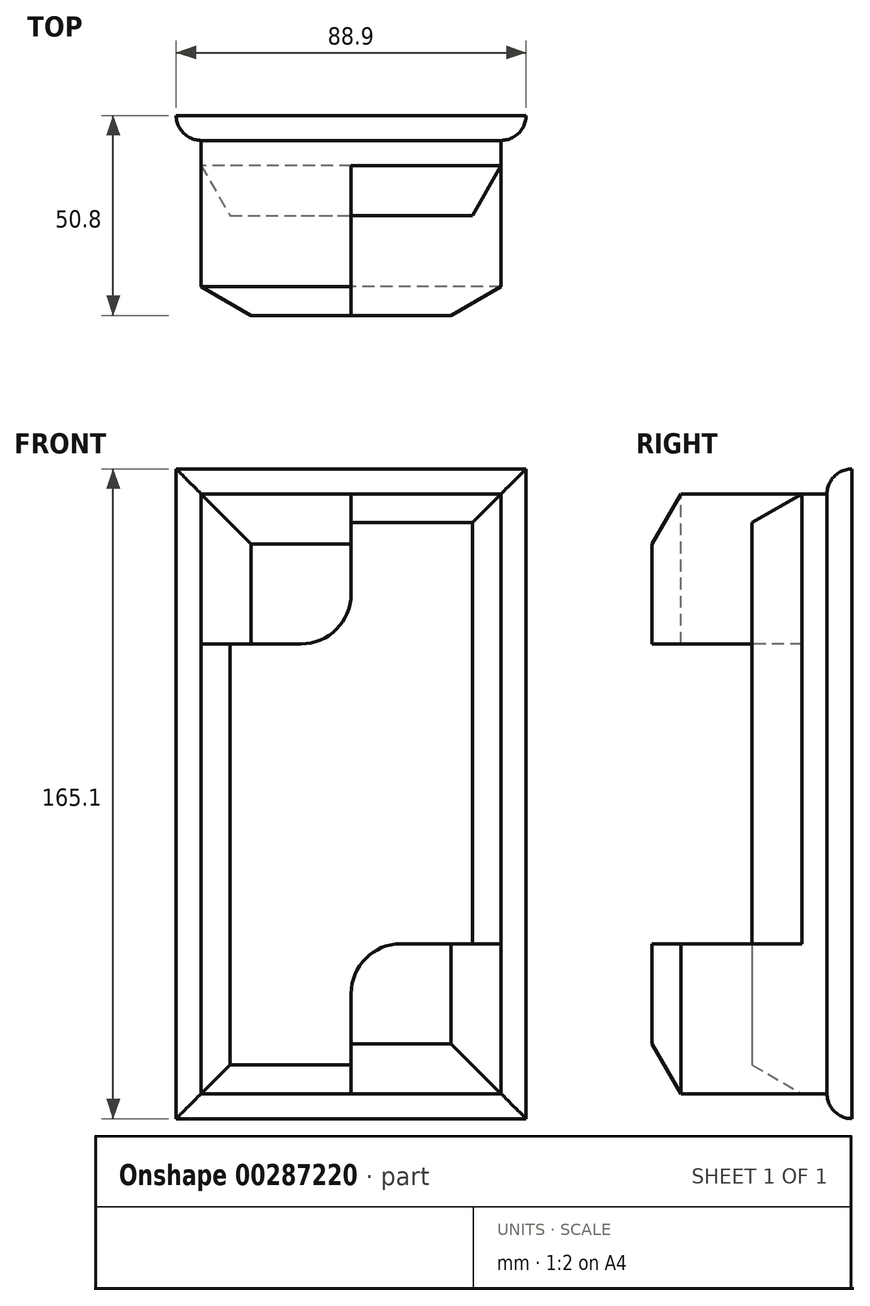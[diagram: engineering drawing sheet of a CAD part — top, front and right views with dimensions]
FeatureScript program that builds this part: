
annotation { "Feature Type Name" : "Feature", "Feature Type Description" : "" }
export const myFeature = defineFeature(function(context is Context, id is Id, definition is map)
    precondition{}
    {
        {
            var Q0;
            Q0=qCreatedBy(makeId("Front.planeOp"),FACE);
            var sketch = newSketch(context, id + "F0", { "sketchPlane" : qUnion([Q0])});
            skLineSegment(sketch, "E0.bottom", {"start": v(-38.1, 76.2) * mm, "end": v(38.1, 76.2) * mm});
            skLineSegment(sketch, "E0.top", {"start": v(-38.1, -76.2) * mm, "end": v(38.1, -76.2) * mm});
            skLineSegment(sketch, "E0.left", {"start": v(-38.1, 76.2) * mm, "end": v(-38.1, -76.2) * mm});
            skLineSegment(sketch, "E0.right", {"start": v(38.1, 76.2) * mm, "end": v(38.1, -76.2) * mm});
            skPoint(sketch, "E0.middle", {"position": v(0, 0) * mm});
            skLineSegment(sketch, "E1.0", {"start": v(-44.45, -82.55) * mm, "end": v(44.45, -82.55) * mm});
            skLineSegment(sketch, "E1.1", {"start": v(-44.45, 82.55) * mm, "end": v(-44.45, -82.55) * mm});
            skLineSegment(sketch, "E1.2", {"start": v(-44.45, 82.55) * mm, "end": v(44.45, 82.55) * mm});
            skLineSegment(sketch, "E1.3", {"start": v(44.45, 82.55) * mm, "end": v(44.45, -82.55) * mm});
            skLineSegment(sketch, "E2", {"start": v(-38.1, 38.1) * mm, "end": v(-12.7, 38.1) * mm});
            skLineSegment(sketch, "E3", {"start": v(0, 50.8) * mm, "end": v(0, 76.2) * mm});
            skLineSegment(sketch, "E4", {"start": v(38.1, -38.1) * mm, "end": v(12.7, -38.1) * mm});
            skLineSegment(sketch, "E5", {"start": v(0, -50.8) * mm, "end": v(0, -76.2) * mm});
            skPoint(sketch, "E6.visualSharp", {"position": v(0, -38.1) * mm});
            skArc(sketch, "E6.filletArc", {"start": v(12.7, -38.1) * mm, "mid": v(3.72, -41.82) * mm, "end": v(0, -50.8) * mm});
            skPoint(sketch, "E7.visualSharp", {"position": v(0, 38.1) * mm});
            skArc(sketch, "E7.filletArc", {"start": v(-12.7, 38.1) * mm, "mid": v(-3.72, 41.82) * mm, "end": v(0, 50.8) * mm});
            skSolve(sketch);
        }
        {
            var Q0;
            Q0 = qSketchRegion(id + "F0", true);
            extrude(context, id + "F1", {"entities" : qUnion([Q0]), "depth" : 6.35 * mm});
        }
        {
            var Q0;
            {var subQ3=sQuery(id+"F0.wireOp",EDGE,"E2");Q0=makeQuery(id+"F0.imprint","IMPRINT",FACE,{"disambiguationData":[TD([[makeQuery(id+"F0.imprint","IMPRINT",EDGE,{"derivedFrom":subQ3}),-1.0]])]});}
            extrude(context, id + "F2", {"entities" : qUnion([Q0]), "operationType" : NewBodyOperationType.ADD, "depth" : 25.4 * mm});
        }
        {
            var Q0;
            {var subQ1=sQuery(id+"F0.wireOp",EDGE,"E2");Q0=makeQuery(id+"F0.imprint","IMPRINT",FACE,{"disambiguationData":[TD([[makeQuery(id+"F0.imprint","IMPRINT",EDGE,{"derivedFrom":subQ1}),1.0]])]});}
            var Q1;
            {var subQ1=sQuery(id+"F0.wireOp",EDGE,"E4");Q1=makeQuery(id+"F0.imprint","IMPRINT",FACE,{"disambiguationData":[TD([[makeQuery(id+"F0.imprint","IMPRINT",EDGE,{"derivedFrom":subQ1}),1.0]])]});}
            extrude(context, id + "F3", {"entities" : qUnion([Q0, Q1]), "operationType" : NewBodyOperationType.ADD, "depth" : 50.8 * mm});
        }
        {
            var Q0;
            Q0=makeQuery(id+"F3.opExtrude","CAP_EDGE",EDGE,{"disambiguationData":[OSD([sQuery(id+"F0.wireOp",EDGE,"E0.left")])],"isStart":false});
            var Q1;
            Q1=makeQuery(id+"F3.opExtrude","CAP_EDGE",EDGE,{"disambiguationData":[OSD([sQuery(id+"F0.wireOp",EDGE,"E0.top")])],"isStart":false});
            var Q2;
            Q2=makeQuery(id+"F3.opExtrude","CAP_EDGE",EDGE,{"disambiguationData":[OSD([sQuery(id+"F0.wireOp",EDGE,"E0.bottom")])],"isStart":false});
            chamfer(context, id + "F4", {"entities" : qUnion([Q0, Q1, Q2]), "chamferType" : ChamferType.OFFSET_ANGLE, "width" : 12.7 * mm, "oppositeDirection" : false, "angle" : 30 * degree, "tangentPropagation" : true});
        }
        {
            var Q0;
            Q0=makeQuery(id+"F1.opExtrude","CAP_EDGE",EDGE,{"disambiguationData":[OSD([sQuery(id+"F0.wireOp",EDGE,"E1.3")])],"isStart":false});
            var Q1;
            Q1=makeQuery(id+"F1.opExtrude","CAP_EDGE",EDGE,{"disambiguationData":[OSD([sQuery(id+"F0.wireOp",EDGE,"E1.2")])],"isStart":false});
            var Q2;
            Q2=makeQuery(id+"F1.opExtrude","CAP_EDGE",EDGE,{"disambiguationData":[OSD([sQuery(id+"F0.wireOp",EDGE,"E1.1")])],"isStart":false});
            var Q3;
            Q3=makeQuery(id+"F1.opExtrude","CAP_EDGE",EDGE,{"disambiguationData":[OSD([sQuery(id+"F0.wireOp",EDGE,"E1.0")])],"isStart":false});
            fillet(context, id + "F5", {"entities" : qUnion([Q0, Q1, Q2, Q3]), "radius" : 6.35 * mm, "tangentPropagation" : true, "allowEdgeOverflow" : false});
        }
        {
            var Q0;
            Q0=makeQuery(id+"F2.opExtrude","CAP_EDGE",EDGE,{"disambiguationData":[OSD([sQuery(id+"F0.wireOp",EDGE,"E0.right")])],"isStart":false});
            var Q1;
            Q1=makeQuery(id+"F2.opExtrude","CAP_EDGE",EDGE,{"disambiguationData":[OSD([sQuery(id+"F0.wireOp",EDGE,"E0.bottom")])],"isStart":false});
            var Q2;
            Q2=makeQuery(id+"F2.opExtrude","CAP_EDGE",EDGE,{"disambiguationData":[OSD([sQuery(id+"F0.wireOp",EDGE,"E0.left")])],"isStart":false});
            var Q3;
            Q3=makeQuery(id+"F2.opExtrude","CAP_EDGE",EDGE,{"disambiguationData":[OSD([sQuery(id+"F0.wireOp",EDGE,"E0.top")])],"isStart":false});
            chamfer(context, id + "F6", {"entities" : qUnion([Q0, Q1, Q2, Q3]), "chamferType" : ChamferType.OFFSET_ANGLE, "width" : 12.7 * mm, "oppositeDirection" : false, "angle" : 30 * degree, "tangentPropagation" : true});
        }
        {
            var Q0;
            Q0=makeQuery(id+"F3.opExtrude","CAP_EDGE",EDGE,{"disambiguationData":[OSD([sQuery(id+"F0.wireOp",EDGE,"E0.right")])],"isStart":false});
            chamfer(context, id + "F7", {"entities" : qUnion([Q0]), "chamferType" : ChamferType.OFFSET_ANGLE, "width" : 12.7 * mm, "oppositeDirection" : true, "angle" : 30 * degree, "tangentPropagation" : true});
        }
    });
